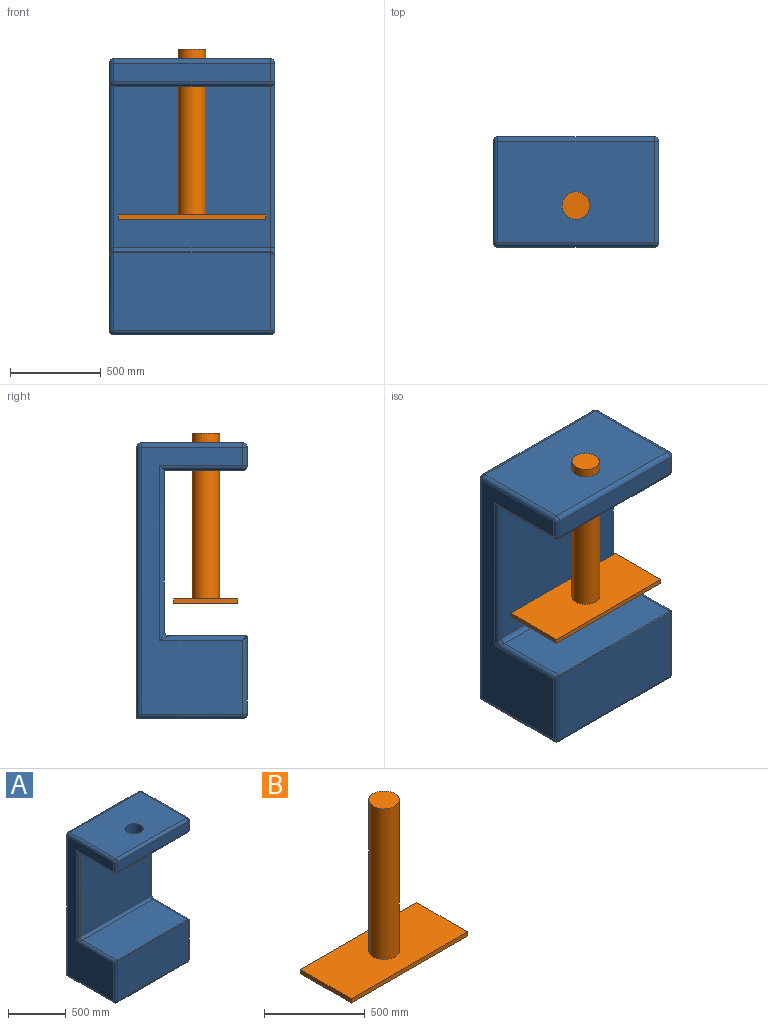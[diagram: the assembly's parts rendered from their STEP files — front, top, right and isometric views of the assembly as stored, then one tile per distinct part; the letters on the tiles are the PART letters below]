
ASSEMBLY  parts=2 mates=1
PART A: 45 faces, bbox 914.4x609.6x1524 mm
  f0: plane 1473.2x558.8mm, normal (1,0,0), area 382488.5mm2, adj f14,f16,f33,f34,f35,f37,f39,f40
  f1: plane 863.6x426.72mm, normal (0,-1,0), area 368515.4mm2, adj f12,f14,f17,f31
  f2: plane 1498.6x863.6mm, normal (0,1,0), area 1294191mm2, adj f6,f20,f34,f43
  f3: plane 1473.2x558.8mm, normal (-1,0,0), area 381934.7mm2, adj f17,f18,f20,f21,f22,f23,f25,f26
  f4: plane 863.6x101.6mm, normal (0,-1,0), area 87741.8mm2, adj f11,f13,f26,f37
  f5: plane 863.6x558.8mm, normal (0,0,1), area 464338.2mm2, adj f10,f11,f22,f35,f43
  f6: plane 863.6x584.2mm, normal (0,0,-1), area 504515.1mm2, adj f2,f18,f31,f33
  f7: plane 863.6x431.8mm, normal (0,0,-1), area 354661mm2, adj f9,f10,f13,f25,f39
  f8: plane 863.6x426.72mm, normal (0,0,1), area 368515.4mm2, adj f12,f16,f21,f28
  f9: plane 889x863.6mm, normal (0,-1,0), area 767740.4mm2, adj f7,f23,f28,f40
  f10: cylinder r=76.2mm len=152.4mm, axis (0,0,1), area 72965.9mm2, adj f5,f7
  f11: cylinder r=25.4mm len=863.6mm, axis (-1,0,0), area 34456.1mm2, adj f4,f5,f24,f36
  f12: cylinder r=5.08mm len=863.6mm, axis (1,0,0), area 6891.2mm2, adj f1,f8,f15,f19
  f13: cylinder r=25.4mm len=863.6mm, axis (-1,0,0), area 34456.1mm2, adj f4,f7,f27,f38
  f14: cylinder r=25.4mm len=426.72mm, axis (0,0,1), area 16730.8mm2, adj f0,f1,f15,f32
  f15: bspline ~29.36x25.4mm, area 219.1mm2, adj f12,f14,f16
  f16: cylinder r=25.4mm len=426.72mm, axis (0,1,0), area 16730.8mm2, adj f0,f8,f15,f41
  f17: cylinder r=25.4mm len=426.72mm, axis (0,0,-1), area 16730.8mm2, adj f1,f3,f19,f30
  f18: cylinder r=25.4mm len=584.2mm, axis (0,-1,0), area 22940.3mm2, adj f3,f6,f20,f30
  f19: bspline ~29.36x25.4mm, area 219.1mm2, adj f12,f17,f21
  f20: cylinder r=25.4mm len=1498.6mm, axis (0,0,1), area 59423.2mm2, adj f2,f3,f18,f44
  f21: cylinder r=25.4mm len=477.52mm, axis (0,-1,0), area 17467.3mm2, adj f3,f8,f19,f29
  f22: cylinder r=25.4mm len=558.8mm, axis (0,1,0), area 22295.1mm2, adj f3,f5,f24,f44
  f23: cylinder r=25.4mm len=965.2mm, axis (0,0,1), area 36574.3mm2, adj f3,f9,f25,f29
  f24: sphere r=25.4mm, area 1013.4mm2, adj f11,f22,f26
  f25: cylinder r=25.4mm len=457.2mm, axis (0,1,0), area 17596.3mm2, adj f3,f7,f23,f27
  f26: cylinder r=25.4mm len=101.6mm, axis (0,0,-1), area 4053.7mm2, adj f3,f4,f24,f27
  f27: sphere r=25.4mm, area 1013.4mm2, adj f13,f25,f26
  f28: cylinder r=25.4mm len=863.6mm, axis (1,0,0), area 34456.1mm2, adj f8,f9,f29,f41
  f29: bspline ~50.8x50.8mm, area 1218.3mm2, adj f21,f23,f28
  f30: sphere r=25.4mm, area 1013.4mm2, adj f17,f18,f31
  f31: cylinder r=25.4mm len=863.6mm, axis (1,0,0), area 34456.1mm2, adj f1,f6,f30,f32
  f32: sphere r=25.4mm, area 1013.4mm2, adj f14,f31,f33
  f33: cylinder r=25.4mm len=584.2mm, axis (0,1,0), area 22940.3mm2, adj f0,f6,f32,f34
  f34: cylinder r=25.4mm len=1498.6mm, axis (0,0,-1), area 59423.2mm2, adj f0,f2,f33,f42
  f35: cylinder r=25.4mm len=558.8mm, axis (0,-1,0), area 22295.1mm2, adj f0,f5,f36,f42
  f36: sphere r=25.4mm, area 1013.4mm2, adj f11,f35,f37
  f37: cylinder r=25.4mm len=101.6mm, axis (0,0,1), area 4053.7mm2, adj f0,f4,f36,f38
  f38: sphere r=25.4mm, area 1013.4mm2, adj f13,f37,f39
  f39: cylinder r=25.4mm len=457.2mm, axis (0,-1,0), area 17596.3mm2, adj f0,f7,f38,f40
  f40: cylinder r=25.4mm len=914.4mm, axis (0,0,-1), area 35837.8mm2, adj f0,f9,f39,f41
  f41: torus R=50.8mm, axis (1,0,0), area 2170.3mm2, adj f0,f16,f28,f40
  f42: sphere r=25.4mm, area 1013.4mm2, adj f34,f35,f43
  f43: cylinder r=25.4mm len=863.6mm, axis (1,0,0), area 34456.1mm2, adj f2,f5,f42,f44
  f44: sphere r=25.4mm, area 1013.4mm2, adj f20,f22,f43
PART B: 8 faces, bbox 812.8x355.6x939.8 mm
  f0: plane 812.8x25.4mm, normal (0,1,0), area 20645.1mm2, adj f1,f3,f4,f5
  f1: plane 355.6x25.4mm, normal (-1,0,0), area 9032.2mm2, adj f0,f2,f4,f5
  f2: plane 812.8x25.4mm, normal (0,-1,0), area 20645.1mm2, adj f1,f3,f4,f5
  f3: plane 355.6x25.4mm, normal (1,0,0), area 9032.2mm2, adj f0,f2,f4,f5
  f4: plane 812.8x355.6mm, normal (0,0,1), area 270790.2mm2, adj f0,f1,f2,f3,f6
  f5: plane 812.8x355.6mm, normal (0,0,-1), area 289031.7mm2, adj f0,f1,f2,f3
  f6: cylinder r=76.2mm len=914.4mm, axis (0,0,-1), area 437795.3mm2, adj f4,f7
  f7: plane 152.4x152.4mm, normal (0,0,1), area 18241.5mm2, adj f6
PLACE A t=(-10.03,-40.49,-52.04)mm fixed
PLACE B t=(15.25,-53.18,584.2)mm
MATE slider B.f6 <-> A.f10  axis (0,0,1) through (18.54,-123.62,1524)mm
